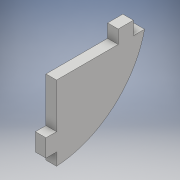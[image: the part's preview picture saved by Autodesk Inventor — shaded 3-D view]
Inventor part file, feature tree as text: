
AUTODESK INVENTOR PART (.ipt)
format: ipt  version: 2017 (Build 210142000, 142)  size: 104,960 bytes
history: native  units: mm
features: extrude x1, sketch x1
ambient origin geometry x8: Origin, YZ Plane, XZ Plane, XY Plane, X Axis, Y Axis, Z Axis, Center Point
bodies: Solide1 (feature_tree)
feature tree (2):
  extrude  "Extrusion1"  Depth=35.0mm
  sketch  "Esquisse1"
